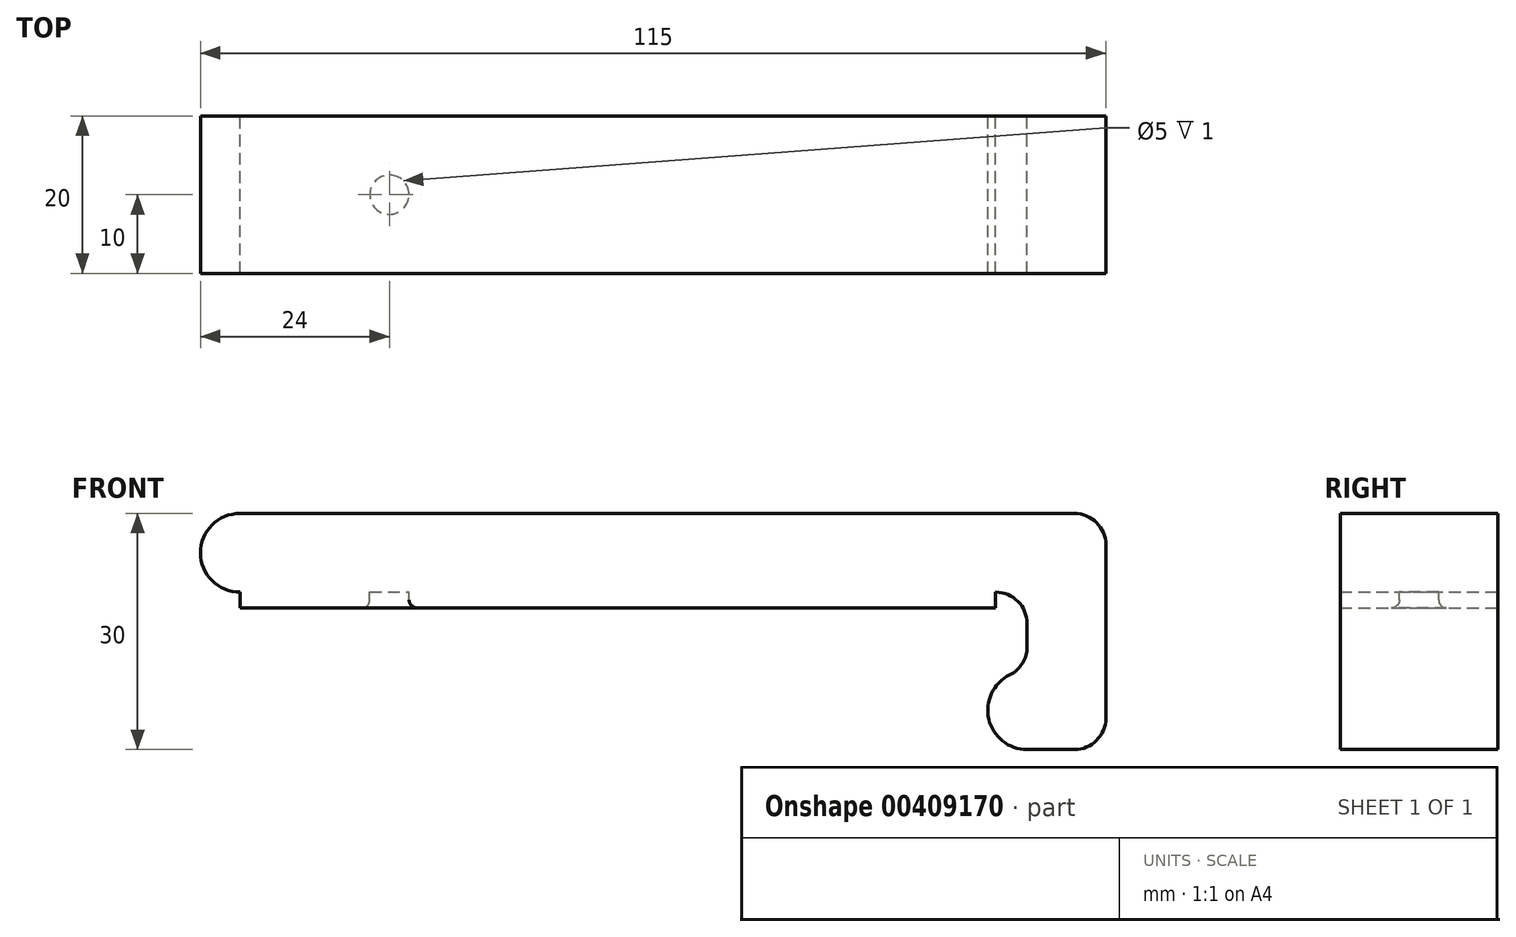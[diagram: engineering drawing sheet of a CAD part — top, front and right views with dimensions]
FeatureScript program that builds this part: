
annotation { "Feature Type Name" : "Feature", "Feature Type Description" : "" }
export const myFeature = defineFeature(function(context is Context, id is Id, definition is map)
    precondition{}
    {
        {
            var Q0;
            Q0=qCreatedBy(makeId("Front.planeOp"),FACE);
            var sketch = newSketch(context, id + "F0", { "sketchPlane" : qUnion([Q0])});
            skLineSegment(sketch, "E0", {"start": v(-52.5, 0) * mm, "end": v(43.5, 0) * mm});
            skLineSegment(sketch, "E1", {"start": v(47.5, -4) * mm, "end": v(47.5, -6.94) * mm});
            skLineSegment(sketch, "E2", {"start": v(47.5, -20) * mm, "end": v(53.5, -20) * mm});
            skLineSegment(sketch, "E3", {"start": v(57.5, -16) * mm, "end": v(57.5, 6) * mm});
            skLineSegment(sketch, "E4", {"start": v(53.5, 10) * mm, "end": v(-52.5, 10) * mm});
            skLineSegment(sketch, "E5", {"start": v(-57.5, 10) * mm, "end": v(-57.5, 0) * mm, "construction": true});
            skArc(sketch, "E6", {"start": v(47.5, -20) * mm, "mid": v(42.63, -16.14) * mm, "end": v(45.28, -10.52) * mm});
            skLineSegment(sketch, "E7", {"start": v(42.5, -4.07) * mm, "end": v(42.5, -24.16) * mm, "construction": true});
            skArc(sketch, "E8", {"start": v(-52.5, 10) * mm, "mid": v(-57.5, 5) * mm, "end": v(-52.5, 0) * mm});
            skPoint(sketch, "E9.visualSharp", {"position": v(57.5, 10) * mm});
            skArc(sketch, "E9.filletArc", {"start": v(57.5, 6) * mm, "mid": v(56.33, 8.83) * mm, "end": v(53.5, 10) * mm});
            skPoint(sketch, "E10.visualSharp", {"position": v(47.5, -10) * mm});
            skArc(sketch, "E10.filletArc", {"start": v(45.28, -10.52) * mm, "mid": v(46.9, -9.05) * mm, "end": v(47.5, -6.94) * mm});
            skPoint(sketch, "E11.visualSharp", {"position": v(47.5, 0) * mm});
            skArc(sketch, "E11.filletArc", {"start": v(47.5, -4) * mm, "mid": v(46.33, -1.17) * mm, "end": v(43.5, 0) * mm});
            skPoint(sketch, "E12.visualSharp", {"position": v(57.5, -20) * mm});
            skArc(sketch, "E12.filletArc", {"start": v(53.5, -20) * mm, "mid": v(56.33, -18.83) * mm, "end": v(57.5, -16) * mm});
            skSolve(sketch);
        }
        {
            var Q0;
            Q0=makeQuery(id+"F0.imprint","IMPRINT",FACE,{"disambiguationData":[TD([[makeQuery(id+"F0.imprint","IMPRINT",EDGE,{"derivedFrom":sQuery(id+"F0.wireOp",EDGE,"E0")}),1.0]])]});
            extrude(context, id + "F1", {"entities" : qUnion([Q0]), "depth" : 20 * mm});
        }
        {
            var Q0;
            Q0=makeQuery(id+"F1.opExtrude","SWEPT_FACE",FACE,{"disambiguationData":[OSD([sQuery(id+"F0.wireOp",EDGE,"E0")])]});
            var sketch = newSketch(context, id + "F2", { "sketchPlane" : qUnion([Q0])});
            skCircle(sketch, "E13", {"center": v(33.5, 10) * mm, "radius": 2.5 * mm});
            skCircle(sketch, "E14", {"center": v(33.5, 10) * mm, "radius": 10 * mm, "construction": true});
            skCircle(sketch, "E15.MirrorC", {"center": v(-33.5, 10) * mm, "radius": 2.5 * mm});
            skSolve(sketch);
        }
        {
            var Q0;
            Q0=makeQuery(id+"F2.imprint","IMPRINT",FACE,{"disambiguationData":[TD([[makeQuery(id+"F2.imprint","IMPRINT",EDGE,{"derivedFrom":sQuery(id+"F2.wireOp",EDGE,"E15.MirrorC")}),-1.0]])]});
            var Q1;
            Q1=makeQuery(id+"F2.imprint","IMPRINT",FACE,{"disambiguationData":[TD([[makeQuery(id+"F2.imprint","IMPRINT",EDGE,{"derivedFrom":sQuery(id+"F2.wireOp",EDGE,"E13")}),1.0]])]});
            extrude(context, id + "F3", {"entities" : qUnion([Q0, Q1]), "operationType" : NewBodyOperationType.ADD, "depth" : 2 * mm});
        }
        {
            var Q0;
            Q0=makeQuery(id+"F3.opExtrude","CAP_EDGE",EDGE,{"disambiguationData":[OSD([sQuery(id+"F2.wireOp",EDGE,"E15.MirrorC")])],"isStart":true});
            var Q1;
            Q1=makeQuery(id+"F3.opExtrude","CAP_EDGE",EDGE,{"disambiguationData":[OSD([sQuery(id+"F2.wireOp",EDGE,"E15.MirrorC")])],"isStart":false});
            var Q2;
            Q2=makeQuery(id+"F3.opExtrude","CAP_EDGE",EDGE,{"disambiguationData":[OSD([sQuery(id+"F2.wireOp",EDGE,"E13")])],"isStart":true});
            var Q3;
            Q3=makeQuery(id+"F3.opExtrude","CAP_EDGE",EDGE,{"disambiguationData":[OSD([sQuery(id+"F2.wireOp",EDGE,"E13")])],"isStart":false});
            fillet(context, id + "F4", {"entities" : qUnion([Q0, Q1, Q2, Q3]), "radius" : 1 * mm, "tangentPropagation" : true, "allowEdgeOverflow" : false});
        }
    });
